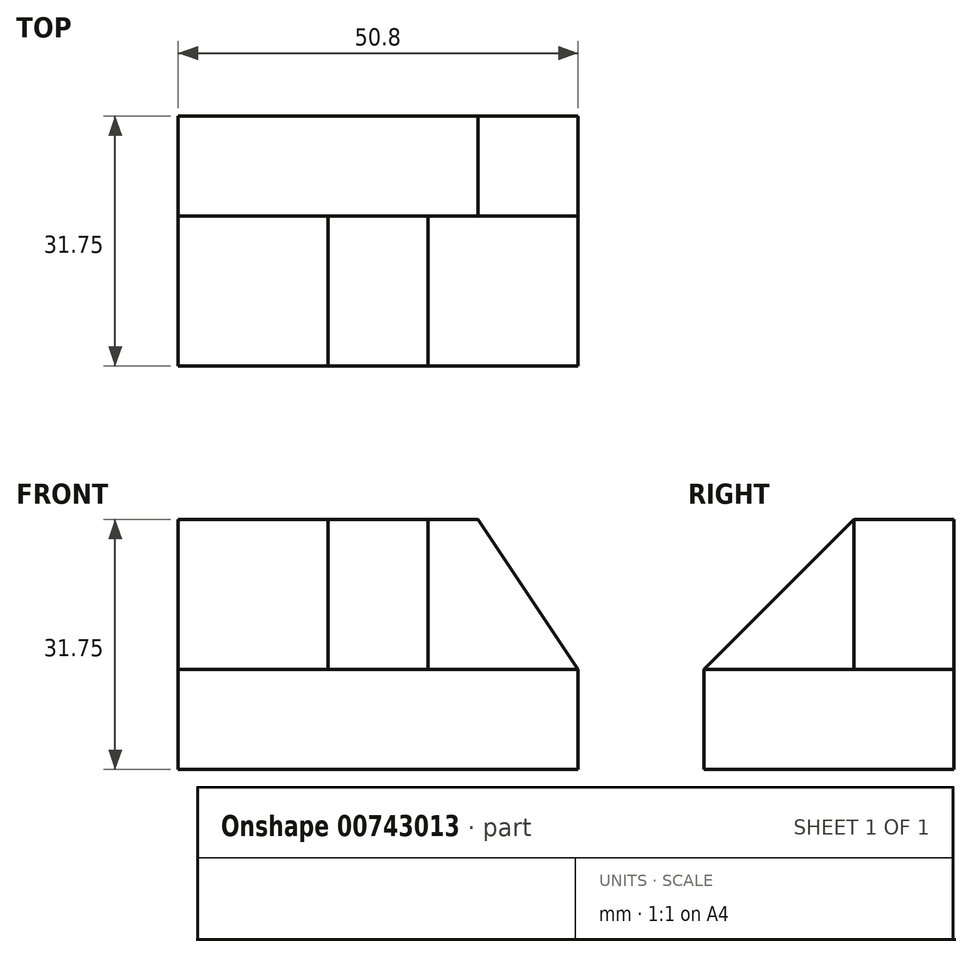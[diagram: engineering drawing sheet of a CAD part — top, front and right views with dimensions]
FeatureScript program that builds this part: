
annotation { "Feature Type Name" : "Feature", "Feature Type Description" : "" }
export const myFeature = defineFeature(function(context is Context, id is Id, definition is map)
    precondition{}
    {
        {
            var Q0;
            Q0=qCreatedBy(makeId("Front.planeOp"),FACE);
            var sketch = newSketch(context, id + "F0", { "sketchPlane" : qUnion([Q0])});
            skLineSegment(sketch, "E0", {"start": v(0, 0) * mm, "end": v(50.8, 0) * mm});
            skLineSegment(sketch, "E1", {"start": v(50.8, 0) * mm, "end": v(50.8, 31.75) * mm});
            skLineSegment(sketch, "E2", {"start": v(50.8, 31.75) * mm, "end": v(0, 31.75) * mm});
            skLineSegment(sketch, "E3", {"start": v(0, 31.75) * mm, "end": v(0, 0) * mm});
            skSolve(sketch);
        }
        {
            var Q0;
            Q0=makeQuery(id+"F0.imprint","IMPRINT",FACE,{"disambiguationData":[TD([[makeQuery(id+"F0.imprint","IMPRINT",EDGE,{"derivedFrom":sQuery(id+"F0.wireOp",EDGE,"E0")}),1.0]])]});
            extrude(context, id + "F1", {"entities" : qUnion([Q0]), "depth" : 31.75 * mm, "offsetDistance" : 25.4 * mm});
        }
        {
            var Q0;
            Q0=makeQuery(id+"F1.opExtrude","CAP_FACE",FACE,{"disambiguationData":[OSD([sQuery(id+"F0.wireOp",EDGE,"E0"),sQuery(id+"F0.wireOp",EDGE,"E1"),sQuery(id+"F0.wireOp",EDGE,"E2"),sQuery(id+"F0.wireOp",EDGE,"E3")])],"isStart":true});
            var sketch = newSketch(context, id + "F2", { "sketchPlane" : qUnion([Q0])});
            skLineSegment(sketch, "E4", {"start": v(-50.8, 12.7) * mm, "end": v(-31.75, 12.7) * mm});
            skLineSegment(sketch, "E5", {"start": v(-31.75, 12.7) * mm, "end": v(-31.75, 31.75) * mm});
            skLineSegment(sketch, "E6", {"start": v(-31.75, 31.75) * mm, "end": v(-50.8, 31.75) * mm});
            skLineSegment(sketch, "E7", {"start": v(-50.8, 31.75) * mm, "end": v(-50.8, 12.7) * mm});
            skSolve(sketch);
        }
        {
            var Q0;
            Q0=makeQuery(id+"F1.opExtrude","CAP_FACE",FACE,{"disambiguationData":[OSD([sQuery(id+"F0.wireOp",EDGE,"E0"),sQuery(id+"F0.wireOp",EDGE,"E1"),sQuery(id+"F0.wireOp",EDGE,"E2"),sQuery(id+"F0.wireOp",EDGE,"E3")])],"isStart":false});
            var sketch = newSketch(context, id + "F3", { "sketchPlane" : qUnion([Q0])});
            skLineSegment(sketch, "E8", {"start": v(19.05, 31.75) * mm, "end": v(19.05, 12.7) * mm});
            skLineSegment(sketch, "E9", {"start": v(19.05, 12.7) * mm, "end": v(0, 12.7) * mm});
            skLineSegment(sketch, "E10", {"start": v(0, 12.7) * mm, "end": v(0, 31.75) * mm});
            skLineSegment(sketch, "E11", {"start": v(0, 31.75) * mm, "end": v(19.05, 31.75) * mm});
            skSolve(sketch);
        }
        {
            var Q0;
            Q0=makeQuery(id+"F3.imprint","IMPRINT",FACE,{"disambiguationData":[TD([[makeQuery(id+"F3.imprint","IMPRINT",EDGE,{"derivedFrom":sQuery(id+"F3.wireOp",EDGE,"E8")}),-1.0]])]});
            extrude(context, id + "F4", {"entities" : qUnion([Q0]), "operationType" : NewBodyOperationType.REMOVE, "oppositeDirection" : true, "depth" : 19.05 * mm, "offsetDistance" : 25.4 * mm});
        }
        {
            var Q0;
            Q0=makeQuery(id+"F1.opExtrude","CAP_FACE",FACE,{"disambiguationData":[OSD([sQuery(id+"F0.wireOp",EDGE,"E0"),sQuery(id+"F0.wireOp",EDGE,"E1"),sQuery(id+"F0.wireOp",EDGE,"E2"),sQuery(id+"F0.wireOp",EDGE,"E3")])],"isStart":false});
            var sketch = newSketch(context, id + "F5", { "sketchPlane" : qUnion([Q0])});
            skLineSegment(sketch, "E12", {"start": v(31.75, 31.75) * mm, "end": v(31.75, 12.7) * mm});
            skLineSegment(sketch, "E13", {"start": v(31.75, 12.7) * mm, "end": v(50.8, 12.7) * mm});
            skLineSegment(sketch, "E14", {"start": v(50.8, 12.7) * mm, "end": v(50.8, 31.75) * mm});
            skLineSegment(sketch, "E15", {"start": v(50.8, 31.75) * mm, "end": v(31.75, 31.75) * mm});
            skSolve(sketch);
        }
        {
            var Q0;
            Q0=makeQuery(id+"F5.imprint","IMPRINT",FACE,{"disambiguationData":[TD([[makeQuery(id+"F5.imprint","IMPRINT",EDGE,{"derivedFrom":sQuery(id+"F5.wireOp",EDGE,"E12")}),1.0]])]});
            extrude(context, id + "F6", {"entities" : qUnion([Q0]), "operationType" : NewBodyOperationType.REMOVE, "oppositeDirection" : true, "depth" : 19.05 * mm, "offsetDistance" : 25.4 * mm});
        }
        {
            var Q0;
            Q0=makeQuery(id+"F6.boolean.opBoolean","COPY",FACE,{"derivedFrom":makeQuery(id+"F6.opExtrude","SWEPT_FACE",FACE,{"disambiguationData":[OSD([sQuery(id+"F5.wireOp",EDGE,"E12")])]})});
            var sketch = newSketch(context, id + "F7", { "sketchPlane" : qUnion([Q0])});
            skLineSegment(sketch, "E16", {"start": v(-31.75, 12.7) * mm, "end": v(-12.7, 31.75) * mm});
            skLineSegment(sketch, "E17", {"start": v(-12.7, 31.75) * mm, "end": v(-12.7, 12.7) * mm});
            skLineSegment(sketch, "E18", {"start": v(-12.7, 12.7) * mm, "end": v(-31.75, 12.7) * mm});
            skSolve(sketch);
        }
        {
            var Q0;
            Q0=makeQuery(id+"F7.imprint","IMPRINT",FACE,{"disambiguationData":[TD([[makeQuery(id+"F7.imprint","IMPRINT",EDGE,{"derivedFrom":sQuery(id+"F7.wireOp",EDGE,"E16")}),1.0]])]});
            extrude(context, id + "F8", {"entities" : qUnion([Q0]), "operationType" : NewBodyOperationType.REMOVE, "oppositeDirection" : true, "depth" : 25.4 * mm, "offsetDistance" : 25.4 * mm});
        }
        {
            var Q0;
            Q0=makeQuery(id+"F6.boolean.opBoolean","COPY",FACE,{"derivedFrom":makeQuery(id+"F6.opExtrude","CAP_FACE",FACE,{"disambiguationData":[OSD([sQuery(id+"F5.wireOp",EDGE,"E12"),sQuery(id+"F5.wireOp",EDGE,"E13"),sQuery(id+"F5.wireOp",EDGE,"E14"),sQuery(id+"F5.wireOp",EDGE,"E15")])],"isStart":false})});
            var sketch = newSketch(context, id + "F9", { "sketchPlane" : qUnion([Q0])});
            skLineSegment(sketch, "E19", {"start": v(38.1, 31.75) * mm, "end": v(50.8, 12.7) * mm});
            skLineSegment(sketch, "E20", {"start": v(50.8, 12.7) * mm, "end": v(50.8, 31.75) * mm});
            skLineSegment(sketch, "E21", {"start": v(50.8, 31.75) * mm, "end": v(38.1, 31.75) * mm});
            skSolve(sketch);
        }
        {
            var Q0;
            Q0=makeQuery(id+"F9.imprint","IMPRINT",FACE,{"disambiguationData":[TD([[makeQuery(id+"F9.imprint","IMPRINT",EDGE,{"derivedFrom":sQuery(id+"F9.wireOp",EDGE,"E19")}),1.0]])]});
            extrude(context, id + "F10", {"entities" : qUnion([Q0]), "operationType" : NewBodyOperationType.REMOVE, "oppositeDirection" : true, "depth" : 25.4 * mm, "offsetDistance" : 25.4 * mm});
        }
    });
